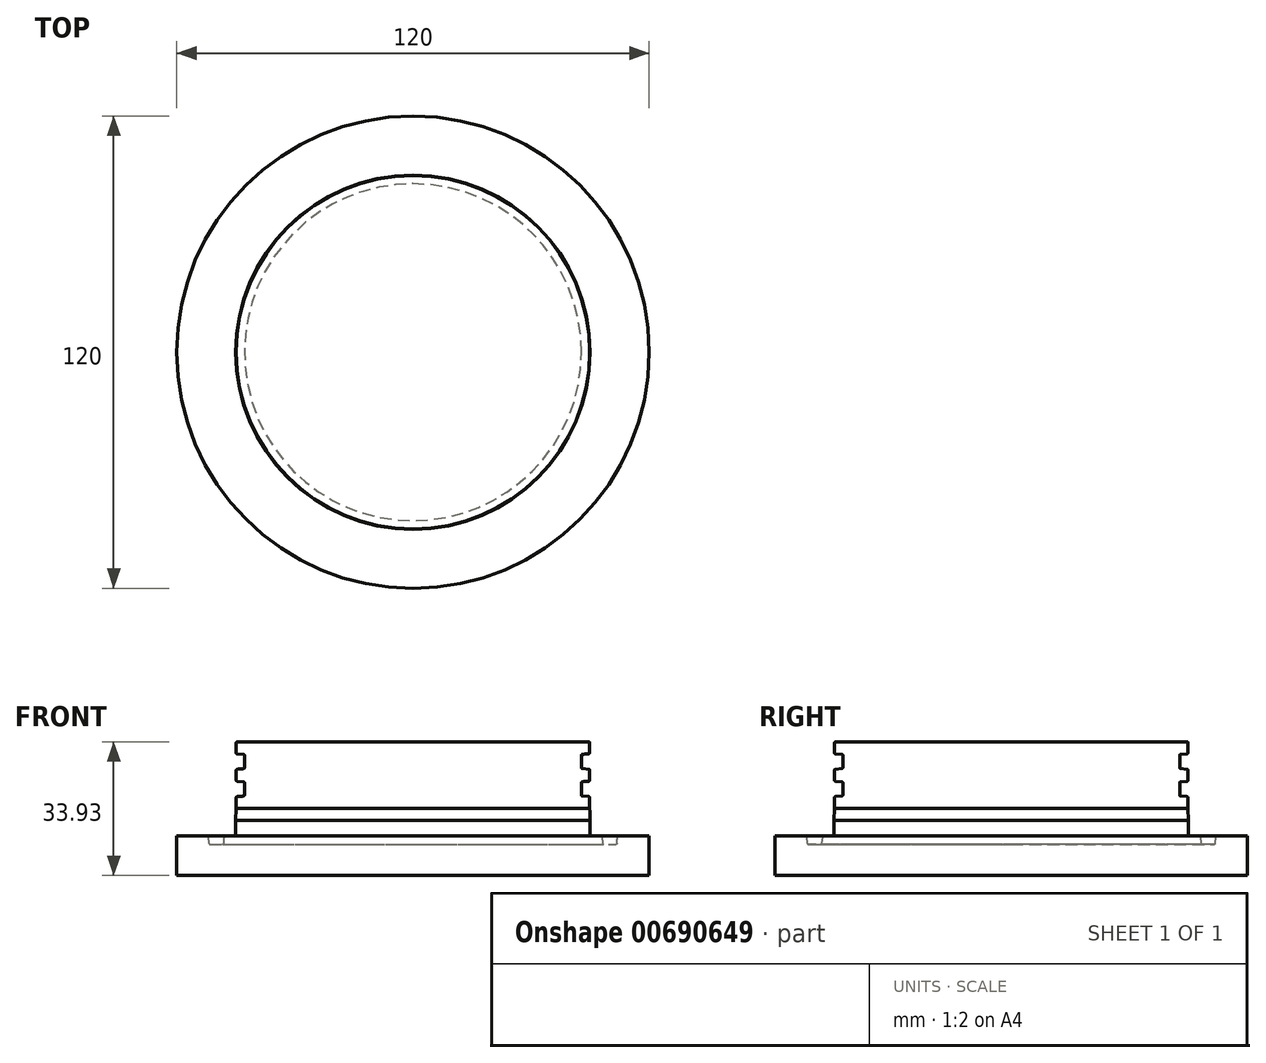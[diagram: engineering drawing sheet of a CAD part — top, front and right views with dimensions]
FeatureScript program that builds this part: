
annotation { "Feature Type Name" : "Feature", "Feature Type Description" : "" }
export const myFeature = defineFeature(function(context is Context, id is Id, definition is map)
    precondition{}
    {
        {
            var Q0;
            Q0=qCreatedBy(makeId("Front.planeOp"),FACE);
            var sketch = newSketch(context, id + "F0", { "sketchPlane" : qUnion([Q0])});
            skLineSegment(sketch, "E0", {"start": v(0, 0) * mm, "end": v(60, 0) * mm});
            skLineSegment(sketch, "E1", {"start": v(60, 0) * mm, "end": v(60, 10) * mm});
            skLineSegment(sketch, "E2", {"start": v(60, 10) * mm, "end": v(51.97, 10) * mm});
            skLineSegment(sketch, "E3", {"start": v(51.97, 10) * mm, "end": v(51.78, 7.9) * mm});
            skLineSegment(sketch, "E4", {"start": v(51.78, 7.9) * mm, "end": v(48.18, 7.9) * mm});
            skLineSegment(sketch, "E5", {"start": v(48.18, 7.9) * mm, "end": v(48, 10) * mm});
            skLineSegment(sketch, "E6", {"start": v(48, 10) * mm, "end": v(45, 10) * mm});
            skLineSegment(sketch, "E7", {"start": v(45, 10) * mm, "end": v(45, 14) * mm});
            skLineSegment(sketch, "E8", {"start": v(45, 14) * mm, "end": v(44.9, 17) * mm});
            skLineSegment(sketch, "E9", {"start": v(44.9, 17) * mm, "end": v(44.9, 20) * mm});
            skLineSegment(sketch, "E10", {"start": v(44.9, 20) * mm, "end": v(42.8, 20.18) * mm});
            skLineSegment(sketch, "E11", {"start": v(42.8, 20.18) * mm, "end": v(42.8, 23.78) * mm});
            skLineSegment(sketch, "E12", {"start": v(42.8, 23.78) * mm, "end": v(44.9, 23.97) * mm});
            skLineSegment(sketch, "E13", {"start": v(44.9, 23.97) * mm, "end": v(44.9, 26.97) * mm});
            skLineSegment(sketch, "E14", {"start": v(44.9, 26.97) * mm, "end": v(42.8, 27.15) * mm});
            skLineSegment(sketch, "E15", {"start": v(42.8, 27.15) * mm, "end": v(42.8, 30.75) * mm});
            skLineSegment(sketch, "E16", {"start": v(42.8, 30.75) * mm, "end": v(44.9, 30.93) * mm});
            skLineSegment(sketch, "E17", {"start": v(44.9, 30.93) * mm, "end": v(44.9, 33.93) * mm});
            skLineSegment(sketch, "E18", {"start": v(44.9, 33.93) * mm, "end": v(0, 33.93) * mm});
            skLineSegment(sketch, "E19", {"start": v(0, 33.93) * mm, "end": v(0, 0) * mm});
            skSolve(sketch);
        }
        {
            var Q0;
            Q0=makeQuery(id+"F0.imprint","IMPRINT",FACE,{"disambiguationData":[TD([[makeQuery(id+"F0.imprint","IMPRINT",EDGE,{"derivedFrom":sQuery(id+"F0.wireOp",EDGE,"E0")}),1.0]])]});
            var Q1;
            Q1=sQuery(id+"F0.wireOp",EDGE,"E19");
            revolve(context, id + "F1", {"entities" : qUnion([Q0]), "axis" : qUnion([Q1]), "revolveType" : RevolveType.FULL});
        }
        {
            var Q0;
            Q0=makeQuery(id+"F1.opRevolve","SWEPT_EDGE",EDGE,{"disambiguationData":[OSD([sQuery(id+"F0.wireOp",EDGE,"E16"),sQuery(id+"F0.wireOp",EDGE,"E17")])]});
            var Q1;
            Q1=makeQuery(id+"F1.opRevolve","SWEPT_EDGE",EDGE,{"disambiguationData":[OSD([sQuery(id+"F0.wireOp",EDGE,"E13"),sQuery(id+"F0.wireOp",EDGE,"E14")])]});
            var Q2;
            Q2=makeQuery(id+"F1.opRevolve","SWEPT_EDGE",EDGE,{"disambiguationData":[OSD([sQuery(id+"F0.wireOp",EDGE,"E12"),sQuery(id+"F0.wireOp",EDGE,"E13")])]});
            var Q3;
            Q3=makeQuery(id+"F1.opRevolve","SWEPT_EDGE",EDGE,{"disambiguationData":[OSD([sQuery(id+"F0.wireOp",EDGE,"E9"),sQuery(id+"F0.wireOp",EDGE,"E10")])]});
            var Q4;
            Q4=makeQuery(id+"F1.opRevolve","SWEPT_EDGE",EDGE,{"disambiguationData":[OSD([sQuery(id+"F0.wireOp",EDGE,"E15"),sQuery(id+"F0.wireOp",EDGE,"E16")])]});
            var Q5;
            Q5=makeQuery(id+"F1.opRevolve","SWEPT_EDGE",EDGE,{"disambiguationData":[OSD([sQuery(id+"F0.wireOp",EDGE,"E11"),sQuery(id+"F0.wireOp",EDGE,"E12")])]});
            var Q6;
            Q6=makeQuery(id+"F1.opRevolve","SWEPT_EDGE",EDGE,{"disambiguationData":[OSD([sQuery(id+"F0.wireOp",EDGE,"E14"),sQuery(id+"F0.wireOp",EDGE,"E15")])]});
            var Q7;
            Q7=makeQuery(id+"F1.opRevolve","SWEPT_EDGE",EDGE,{"disambiguationData":[OSD([sQuery(id+"F0.wireOp",EDGE,"E10"),sQuery(id+"F0.wireOp",EDGE,"E11")])]});
            var Q8;
            Q8=makeQuery(id+"F1.opRevolve","SWEPT_EDGE",EDGE,{"disambiguationData":[OSD([sQuery(id+"F0.wireOp",EDGE,"E4"),sQuery(id+"F0.wireOp",EDGE,"E5")])]});
            var Q9;
            Q9=makeQuery(id+"F1.opRevolve","SWEPT_EDGE",EDGE,{"disambiguationData":[OSD([sQuery(id+"F0.wireOp",EDGE,"E3"),sQuery(id+"F0.wireOp",EDGE,"E4")])]});
            var Q10;
            Q10=makeQuery(id+"F1.opRevolve","SWEPT_EDGE",EDGE,{"disambiguationData":[OSD([sQuery(id+"F0.wireOp",EDGE,"E2"),sQuery(id+"F0.wireOp",EDGE,"E3")])]});
            var Q11;
            Q11=makeQuery(id+"F1.opRevolve","SWEPT_EDGE",EDGE,{"disambiguationData":[OSD([sQuery(id+"F0.wireOp",EDGE,"E5"),sQuery(id+"F0.wireOp",EDGE,"E6")])]});
            var Q12;
            Q12=makeQuery(id+"F1.opRevolve","SWEPT_EDGE",EDGE,{"disambiguationData":[OSD([sQuery(id+"F0.wireOp",EDGE,"E17"),sQuery(id+"F0.wireOp",EDGE,"E18")])]});
            fillet(context, id + "F2", {"entities" : qUnion([Q0, Q1, Q2, Q3, Q4, Q5, Q6, Q7, Q8, Q9, Q10, Q11, Q12]), "radius" : 0.25 * mm, "tangentPropagation" : true, "allowEdgeOverflow" : false});
        }
    });
